# Revit family: PS-S63T z
name_source: partatom
category: Generic Models
revit_build: Autodesk Revit 2016 (Build: 20150220_1215(x64)
units: mm (PartAtom-declared; Revit-internal decimal feet)

## family parameters
Can host rebar = No
Cut with Voids When Loaded = No
Host = Face
Part Type = Normal
Room Calculation Point = No
Round Connector Dimension = Use Diameter
Shared = No

## types (1)
- Default
    100V Taps = 15, 30, 60
    70V Taps = 7.5, 15, 30, 60
    Coverage Horizontal = 90
    Coverage Vertical = 90
    Default Elevation = 48 "
    Depth = 6.86
    Description = 6.5" 2-way White Surface Mount Speaker with 70V/100V transformer for commercial applications
    Directivity (DI) = 7.9
    Directivity Factor (Q) = 6.5
    Environmental = Conforms to MIL-STD-810 for humidity, salt spray, temperature, IEC 529 IPX4 splash-proof rating
    Frequency Range (-10dB) = 49Hz-25kHz
    Frequency Range (-3dB) = 65Hz-20kHz
    Height = 12.14
    High-Frequency Driver = 1” (25mm) Cloth Dome, Pivoting, Ferrofluid cooled
    Impedance = 8
    Input Connector = Front-mounted four pin Euroblock with loop output connections
    Low-Frequency Driver = 6.5” (165mm) Polypropylene Cone, Butyl Rubber Surround
    Manufacturer = Sonance
    Manufacturer URL = http://www.sonance.com
    Model = PS-S63T
    Mounting Bracket = U-Bracket with Sonance FastMount
    Part Number = 45144
    Power Handling = 120
    Power Peak = 120
    Product Documentation Link = https://www.sonance.com
    Product Page URL = https://www.sonance.com
    Regulatory Compliance = UL 1480, UL 2239
    SPL Max = 108
    Sensitivity = 88
    Speaker Data Link = https://www.sonance.com
    Weight Dimensional = 15.63
    Weight Product = 11.43
    Width = 7.51

## geometry (parser evidence)
native form markers: Sweep x3
no freeform markers — native parametric forms only
